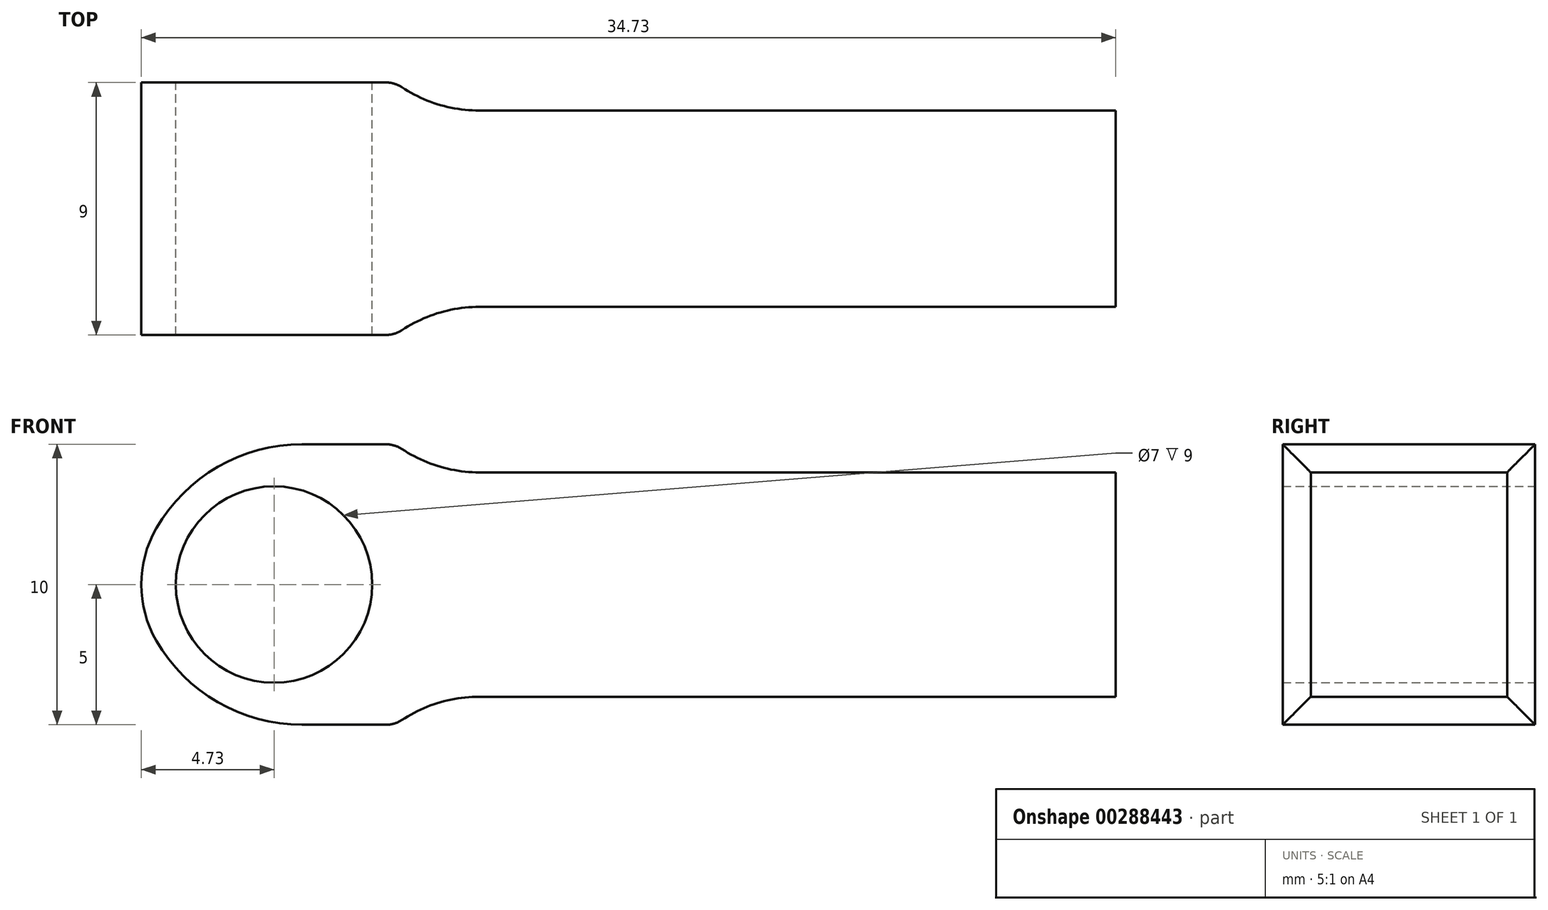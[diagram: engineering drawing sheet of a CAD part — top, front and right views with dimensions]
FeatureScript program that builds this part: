
annotation { "Feature Type Name" : "Feature", "Feature Type Description" : "" }
export const myFeature = defineFeature(function(context is Context, id is Id, definition is map)
    precondition{}
    {
        {
            var Q0;
            Q0=qCreatedBy(makeId("Top.planeOp"),FACE);
            var sketch = newSketch(context, id + "F0", { "sketchPlane" : qUnion([Q0])});
            skLineSegment(sketch, "E0.bottom", {"start": v(5, -4.5) * mm, "end": v(-5, -4.5) * mm});
            skLineSegment(sketch, "E0.top", {"start": v(5, 4.5) * mm, "end": v(-5, 4.5) * mm});
            skLineSegment(sketch, "E0.left", {"start": v(5, -4.5) * mm, "end": v(5, 4.5) * mm});
            skLineSegment(sketch, "E0.right", {"start": v(-5, -4.5) * mm, "end": v(-5, 4.5) * mm});
            skPoint(sketch, "E0.middle", {"position": v(0, 0) * mm});
            skSolve(sketch);
        }
        {
            var Q0;
            Q0 = qSketchRegion(id + "F0", true);
            extrude(context, id + "F1", {"entities" : qUnion([Q0]), "endBound" : BoundingType.SYMMETRIC, "depth" : 10 * mm});
        }
        {
            var Q0;
            Q0=makeQuery(id+"F1.opExtrude","SWEPT_FACE",FACE,{"disambiguationData":[OSD([sQuery(id+"F0.wireOp",EDGE,"E0.top")])]});
            var sketch = newSketch(context, id + "F2", { "sketchPlane" : qUnion([Q0])});
            skPoint(sketch, "E1", {"position": v(0, 0) * mm});
            skSolve(sketch);
        }
        {
            var Q0;
            Q0=sQuery(id+"F2.wireOp",VERTEX,"E1");
            var Q1;
            Q1=makeQuery(id+"F1.opExtrude","SWEPT_BODY",BODY,{"disambiguationData":[OSD([sQuery(id+"F0.wireOp",EDGE,"E0.bottom"),sQuery(id+"F0.wireOp",EDGE,"E0.top"),sQuery(id+"F0.wireOp",EDGE,"E0.left"),sQuery(id+"F0.wireOp",EDGE,"E0.right")])]});
            hole(context, id + "F3", {"style" : HoleStyle.SIMPLE, "endStyle" : HoleEndStyle.THROUGH, "holeDiameter" : 7 * mm, "tappedDepth" : 12 * mm, "tapClearance" : 3, "locations" : qUnion([Q0]), "scope" : qUnion([Q1])});
        }
        {
            var Q0;
            Q0=makeQuery(id+"F1.opExtrude","CAP_EDGE",EDGE,{"disambiguationData":[OSD([sQuery(id+"F0.wireOp",EDGE,"E0.right")])],"isStart":false});
            var Q1;
            Q1=makeQuery(id+"F1.opExtrude","CAP_EDGE",EDGE,{"disambiguationData":[OSD([sQuery(id+"F0.wireOp",EDGE,"E0.right")])],"isStart":true});
            fillet(context, id + "F4", {"entities" : qUnion([Q0, Q1]), "radius" : 6 * mm, "tangentPropagation" : true, "allowEdgeOverflow" : false});
        }
        {
            var Q0;
            Q0=makeQuery(id+"F1.opExtrude","SWEPT_FACE",FACE,{"disambiguationData":[OSD([sQuery(id+"F0.wireOp",EDGE,"E0.left")])]});
            fillet(context, id + "F5", {"entities" : qUnion([Q0]), "radius" : 1 * mm, "tangentPropagation" : true, "allowEdgeOverflow" : false});
        }
        {
            var Q0;
            Q0=makeQuery(id+"F1.opExtrude","SWEPT_FACE",FACE,{"disambiguationData":[OSD([sQuery(id+"F0.wireOp",EDGE,"E0.left")])]});
            var sketch = newSketch(context, id + "F6", { "sketchPlane" : qUnion([Q0])});
            skLineSegment(sketch, "E2.bottom", {"start": v(3.5, -4) * mm, "end": v(-3.5, -4) * mm});
            skLineSegment(sketch, "E2.top", {"start": v(3.5, 4) * mm, "end": v(-3.5, 4) * mm});
            skLineSegment(sketch, "E2.left", {"start": v(3.5, -4) * mm, "end": v(3.5, 4) * mm});
            skLineSegment(sketch, "E2.right", {"start": v(-3.5, -4) * mm, "end": v(-3.5, 4) * mm});
            skPoint(sketch, "E2.middle", {"position": v(0, 0) * mm});
            skSolve(sketch);
        }
        {
            var Q0;
            Q0 = qSketchRegion(id + "F6", true);
            extrude(context, id + "F7", {"entities" : qUnion([Q0]), "operationType" : NewBodyOperationType.ADD, "depth" : 25 * mm});
        }
        {
            var Q0;
            {var subQ0=sQuery(id+"F0.wireOp",EDGE,"E0.left");Q0=makeQuery(id+"F7.boolean.opBoolean","MERGE",EDGE,{"derivedFrom":[makeQuery(id+"F5.opFillet","BLEND_EDGE",EDGE,{"blendedFrom":[makeQuery(id+"F1.opExtrude","CAP_EDGE",EDGE,{"disambiguationData":[OSD([subQ0])],"isStart":false}),makeQuery(id+"F1.opExtrude","SWEPT_FACE",FACE,{"disambiguationData":[OSD([subQ0])]})],"blendedInto":[makeQuery(id+"F1.opExtrude","SWEPT_FACE",FACE,{"disambiguationData":[OSD([subQ0])]})]}),makeQuery(id+"F7.opExtrude","CAP_EDGE",EDGE,{"disambiguationData":[OSD([sQuery(id+"F6.wireOp",EDGE,"E2.top")])],"isStart":true})]});}
            var Q1;
            {var subQ0=sQuery(id+"F0.wireOp",EDGE,"E0.left");Q1=makeQuery(id+"F7.boolean.opBoolean","MERGE",EDGE,{"derivedFrom":[makeQuery(id+"F5.opFillet","BLEND_EDGE",EDGE,{"blendedFrom":[makeQuery(id+"F1.opExtrude","SWEPT_EDGE",EDGE,{"disambiguationData":[OSD([sQuery(id+"F0.wireOp",EDGE,"E0.bottom"),subQ0])]}),makeQuery(id+"F1.opExtrude","SWEPT_FACE",FACE,{"disambiguationData":[OSD([subQ0])]})],"blendedInto":[makeQuery(id+"F1.opExtrude","SWEPT_FACE",FACE,{"disambiguationData":[OSD([subQ0])]})]}),makeQuery(id+"F7.opExtrude","CAP_EDGE",EDGE,{"disambiguationData":[OSD([sQuery(id+"F6.wireOp",EDGE,"E2.right")])],"isStart":true})]});}
            var Q2;
            {var subQ0=sQuery(id+"F0.wireOp",EDGE,"E0.left");Q2=makeQuery(id+"F7.boolean.opBoolean","MERGE",EDGE,{"derivedFrom":[makeQuery(id+"F5.opFillet","BLEND_EDGE",EDGE,{"blendedFrom":[makeQuery(id+"F1.opExtrude","SWEPT_EDGE",EDGE,{"disambiguationData":[OSD([sQuery(id+"F0.wireOp",EDGE,"E0.top"),subQ0])]}),makeQuery(id+"F1.opExtrude","SWEPT_FACE",FACE,{"disambiguationData":[OSD([subQ0])]})],"blendedInto":[makeQuery(id+"F1.opExtrude","SWEPT_FACE",FACE,{"disambiguationData":[OSD([subQ0])]})]}),makeQuery(id+"F7.opExtrude","CAP_EDGE",EDGE,{"disambiguationData":[OSD([sQuery(id+"F6.wireOp",EDGE,"E2.left")])],"isStart":true})]});}
            var Q3;
            {var subQ0=sQuery(id+"F0.wireOp",EDGE,"E0.left");Q3=makeQuery(id+"F7.boolean.opBoolean","MERGE",EDGE,{"derivedFrom":[makeQuery(id+"F5.opFillet","BLEND_EDGE",EDGE,{"blendedFrom":[makeQuery(id+"F1.opExtrude","CAP_EDGE",EDGE,{"disambiguationData":[OSD([subQ0])],"isStart":true}),makeQuery(id+"F1.opExtrude","SWEPT_FACE",FACE,{"disambiguationData":[OSD([subQ0])]})],"blendedInto":[makeQuery(id+"F1.opExtrude","SWEPT_FACE",FACE,{"disambiguationData":[OSD([subQ0])]})]}),makeQuery(id+"F7.opExtrude","CAP_EDGE",EDGE,{"disambiguationData":[OSD([sQuery(id+"F6.wireOp",EDGE,"E2.bottom")])],"isStart":true})]});}
            fillet(context, id + "F8", {"entities" : qUnion([Q0, Q1, Q2, Q3]), "radius" : 5 * mm, "tangentPropagation" : true, "allowEdgeOverflow" : false});
        }
        {
            var Q0;
            {var subQ0=sQuery(id+"F0.wireOp",EDGE,"E0.right");Q0=makeQuery(id+"F4.opFillet","BLEND_EDGE",EDGE,{"blendedFrom":[makeQuery(id+"F1.opExtrude","CAP_EDGE",EDGE,{"disambiguationData":[OSD([subQ0])],"isStart":true}),makeQuery(id+"F1.opExtrude","CAP_EDGE",EDGE,{"disambiguationData":[OSD([subQ0])],"isStart":false})],"blendedInto":[]});}
            fillet(context, id + "F9", {"entities" : qUnion([Q0]), "radius" : 4 * mm, "tangentPropagation" : true, "allowEdgeOverflow" : false});
        }
    });
